# Revit family: en-halla-lina-accessories-recessedrfa
name_source: partatom
category: Специальное оборудование
revit_build: Autodesk Revit 2017 (Build: 20160225_1515(x64)
units: mm (PartAtom-declared; Revit-internal decimal feet)

## family parameters
Заголовок OmniClass = General Luminaries, Non Directional
Номер OmniClass = 23.80.70.11.11
Общий = Нет
Основа = Грань
При загрузке вырезать с полостями = Нет
Размер круглого соединителя = Использовать диаметр
Тип детали = Нормальный
Точка расчета площади = Нет

## types (4) — shared parameters
Lighting height = 145 мм
Lighting length = 1000 мм
Lighting width = 104 мм
Material of luminaire = Aluminium
Odsazení výřezu otvoru = 4 мм
Odsazení zavěšení od osy = 300 мм
URL = www.halla.cz
Изготовитель = HALLA
Код по классификатору = D5020200
Отметка по умолчанию = 1000 мм

## per-type parameters (varying)
| type | Colour of luminaire | L | Ořez L | Ořez tubus | QR code | Tubus |
| 03-0029, E - joint T, metal | Aluminium - anodised | Да | 0 мм | 200 мм |  | Нет |
| 03-0029, W - joint T, metal | Aluminium - white | Да | 0 мм | 200 мм | http://file-system.ru | Нет |
| 03-0017, E - body profile 1000mm | Aluminium - anodised | Нет | 200 мм | 0 мм |  | Да |
| 03-0017, W - body profile 1000mm | Aluminium - white | Нет | 200 мм | 0 мм |  | Да |
